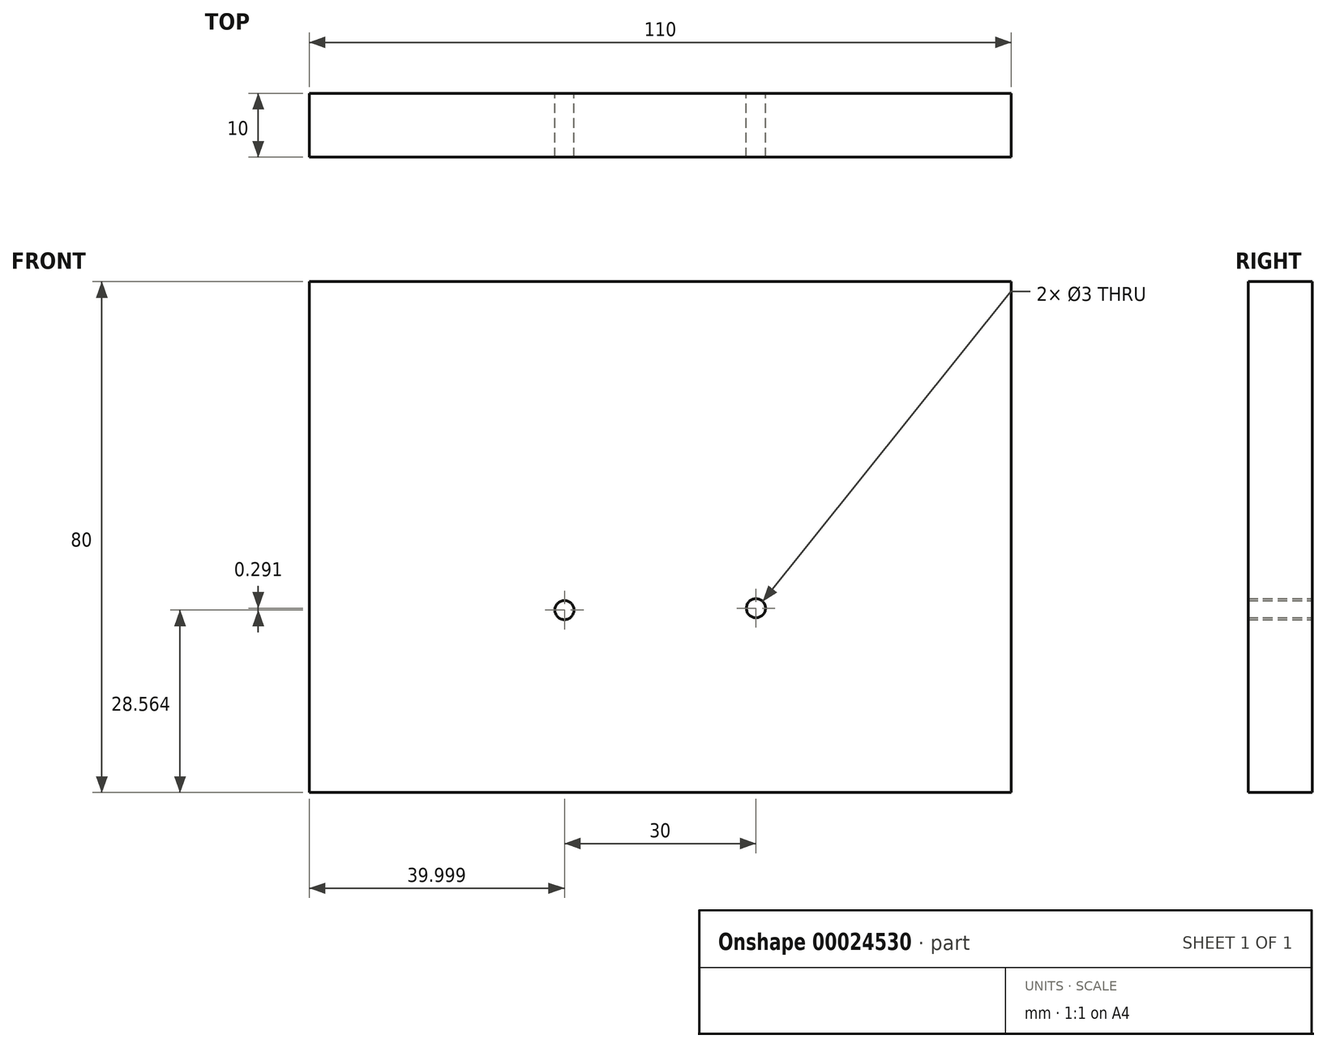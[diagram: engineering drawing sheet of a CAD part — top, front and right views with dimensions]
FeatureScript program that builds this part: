
annotation { "Feature Type Name" : "Feature", "Feature Type Description" : "" }
export const myFeature = defineFeature(function(context is Context, id is Id, definition is map)
    precondition{}
    {
        {
            var Q0;
            Q0=qCreatedBy(makeId("Front.planeOp"),FACE);
            var sketch = newSketch(context, id + "F0", { "sketchPlane" : qUnion([Q0])});
            skLineSegment(sketch, "E0", {"start": v(-84.4, 32.15) * mm, "end": v(-84.4, -47.85) * mm});
            skLineSegment(sketch, "E1", {"start": v(-84.4, -47.85) * mm, "end": v(25.6, -47.85) * mm});
            skLineSegment(sketch, "E2", {"start": v(25.6, -47.85) * mm, "end": v(25.6, 32.15) * mm});
            skLineSegment(sketch, "E3", {"start": v(25.6, 32.15) * mm, "end": v(-84.4, 32.15) * mm});
            skCircle(sketch, "E4", {"center": v(-44.4, -19.29) * mm, "radius": 1.5 * mm});
            skCircle(sketch, "E5", {"center": v(-14.4, -19) * mm, "radius": 1.5 * mm});
            skSolve(sketch);
        }
        {
            var Q0;
            Q0 = qSketchRegion(id + "F0", true);
            extrude(context, id + "F1", {"entities" : qUnion([Q0]), "depth" : 10 * mm});
        }
    });
